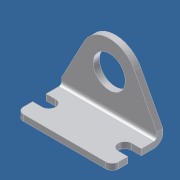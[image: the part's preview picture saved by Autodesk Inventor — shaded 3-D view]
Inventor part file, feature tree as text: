
AUTODESK INVENTOR PART (.ipt)
format: ipt  version: 2012 (Build 160160000, 160)  size: 154,624 bytes
history: native  units: in
note: dims shown in document units (in); Inventor stores cm internally (conversion verified against a paired STEP export)
features: other x126, extrude x7, sketch x7
ambient origin geometry x8: Origin, YZ Plane, XZ Plane, XY Plane, X Axis, Y Axis, Z Axis, Center Point
bodies: Solid1 (feature_tree)
feature tree (140):
  extrude  "Extrusion1"  Depth=0.18in TaperAngle=0.0deg
  extrude  "Extrusion2"  Depth=0.18in TaperAngle=0.0deg
  extrude  "Extrusion3"  Depth=0.18in TaperAngle=0.0deg
  extrude  "Extrusion4"  [1 undecoded]
  extrude  "Extrusion5"  [1 undecoded]
  extrude  "Extrusion6"  [1 undecoded]
  extrude  "Extrusion7"  [1 undecoded]
  other  "h1_XY"
  other  "h1_YZ"
  other  "h1_ZX"
  other  "h1_X"
  other  "h1_Y"
  other  "h1_Z"
  other  "h1_Center"
  other  "d1_XY"
  other  "d1_YZ"
  other  "d1_ZX"
  other  "d1_X"
  other  "d1_Y"
  other  "d1_Z"
  other  "d1_Center"
  other  "h2_XY"
  other  "h2_YZ"
  other  "h2_ZX"
  other  "h2_X"
  other  "h2_Y"
  other  "h2_Z"
  other  "h2_Center"
  other  "d2_XY"
  other  "d2_YZ"
  other  "d2_ZX"
  other  "d2_X"
  other  "d2_Y"
  other  "d2_Z"
  other  "d2_Center"
  other  "h3_XY"
  other  "h3_YZ"
  other  "h3_ZX"
  other  "h3_X"
  other  "h3_Y"
  other  "h3_Z"
  other  "h3_Center"
  other  "h4_XY"
  other  "h4_YZ"
  other  "h4_ZX"
  other  "h4_X"
  other  "h4_Y"
  other  "h4_Z"
  other  "h4_Center"
  other  "h5_XY"
  other  "h5_YZ"
  other  "h5_ZX"
  other  "h5_X"
  other  "h5_Y"
  other  "h5_Z"
  other  "h5_Center"
  other  "h6_XY"
  other  "h6_YZ"
  other  "h6_ZX"
  other  "h6_X"
  other  "h6_Y"
  other  "h6_Z"
  other  "h6_Center"
  other  "l1_XY"
  other  "l1_YZ"
  other  "l1_ZX"
  other  "l1_X"
  other  "l1_Y"
  other  "l1_Z"
  other  "l1_Center"
  other  "l2_XY"
  other  "l2_YZ"
  other  "l2_ZX"
  other  "l2_X"
  other  "l2_Y"
  other  "l2_Z"
  other  "l2_Center"
  other  "l3_XY"
  other  "l3_YZ"
  other  "l3_ZX"
  other  "l3_X"
  other  "l3_Y"
  other  "l3_Z"
  other  "l3_Center"
  other  "l4_XY"
  other  "l4_YZ"
  other  "l4_ZX"
  other  "l4_X"
  other  "l4_Y"
  other  "l4_Z"
  other  "l4_Center"
  other  "l5_XY"
  other  "l5_YZ"
  other  "l5_ZX"
  other  "l5_X"
  other  "l5_Y"
  other  "l5_Z"
  other  "l5_Center"
  other  "l6_XY"
  other  "l6_YZ"
  other  "l6_ZX"
  other  "l6_X"
  other  "l6_Y"
  other  "l6_Z"
  other  "l6_Center"
  other  "l7_XY"
  other  "l7_YZ"
  other  "l7_ZX"
  other  "l7_X"
  other  "l7_Y"
  other  "l7_Z"
  other  "l7_Center"
  other  "l8_XY"
  other  "l8_YZ"
  other  "l8_ZX"
  other  "l8_X"
  other  "l8_Y"
  other  "l8_Z"
  other  "l8_Center"
  other  "mounting_bracket_XY"
  other  "mounting_bracket_YZ"
  other  "mounting_bracket_ZX"
  other  "mounting_bracket_X"
  other  "mounting_bracket_Y"
  other  "mounting_bracket_Z"
  other  "mounting_bracket_Center"
  other  "mounting_bracket_1_XY"
  other  "mounting_bracket_1_YZ"
  other  "mounting_bracket_1_ZX"
  other  "mounting_bracket_1_X"
  other  "mounting_bracket_1_Y"
  other  "mounting_bracket_1_Z"
  other  "mounting_bracket_1_Center"
  sketch  "Sketch_1"  dims[d0=1.875in d1=0.0in d2=0.18in d3=0.0in]
  sketch  "Sketch_2"  dims[d4=0.18in d5=0.0in d6=0.18in d7=0.0in]
  sketch  "Sketch_3"  dims[d8=0.18in d9=0.0in d10=0.18in d11=0.0in]
  sketch  "Sketch_6"  dims[d12=0.18in d13=0.0in]
  sketch  "Sketch_7"
  sketch  "Sketch_8"
  sketch  "Sketch_9"
note: 4 required parameter values undecoded (feature->parameter linkage not recoverable at this tier; creation-order binding heuristic only, values carry confidence <= 0.55)
